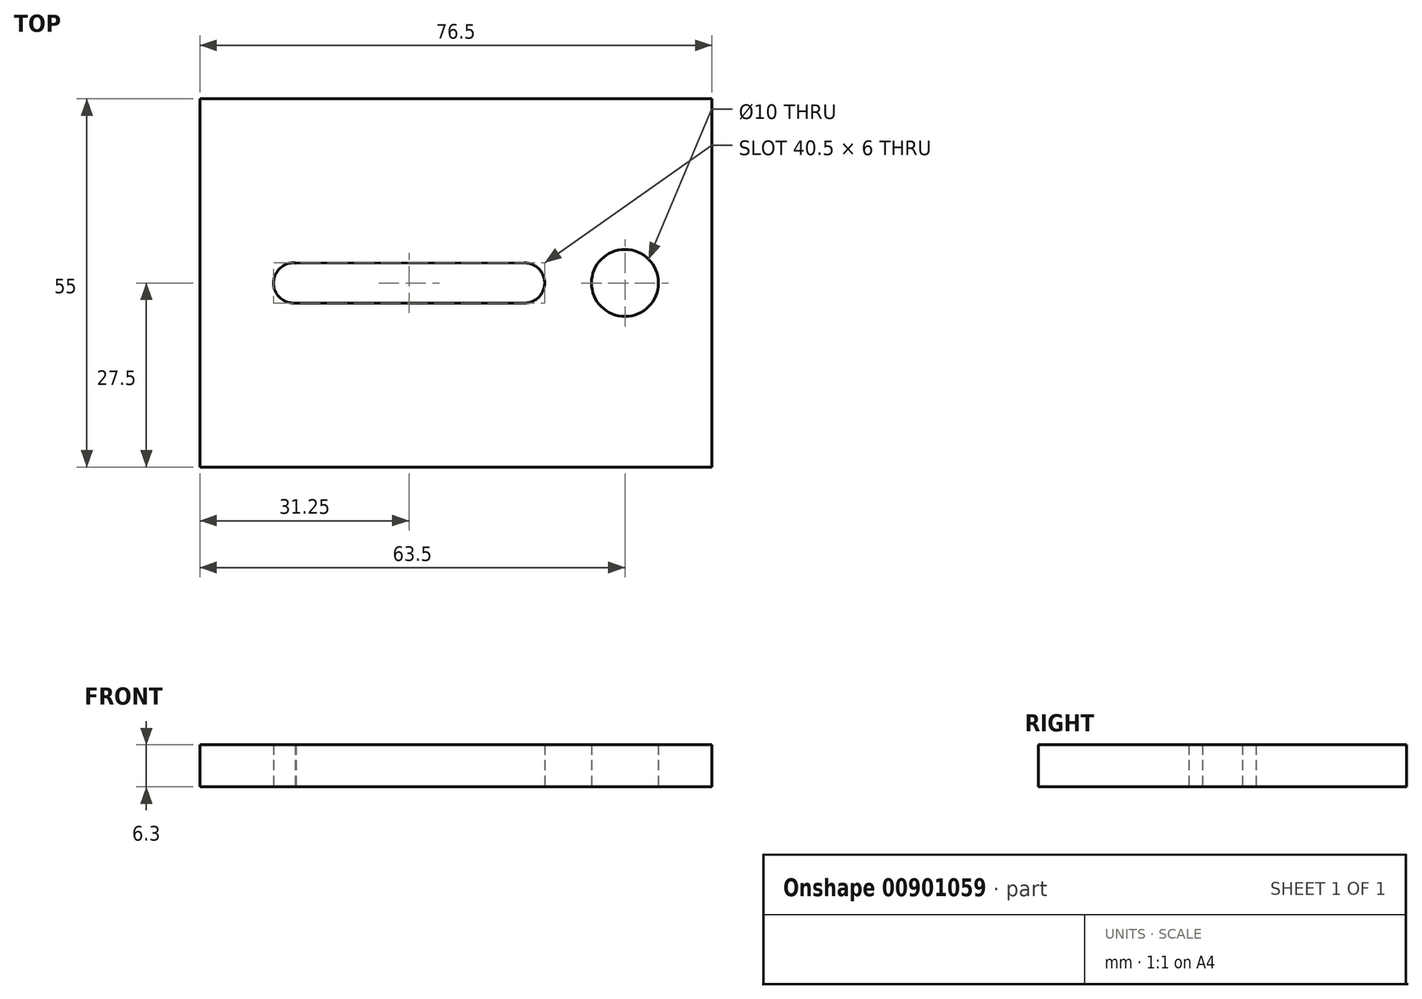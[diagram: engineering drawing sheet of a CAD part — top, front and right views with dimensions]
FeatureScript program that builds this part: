
annotation { "Feature Type Name" : "Feature", "Feature Type Description" : "" }
export const myFeature = defineFeature(function(context is Context, id is Id, definition is map)
    precondition{}
    {
        {
            var Q0;
            Q0=qCreatedBy(makeId("Top.planeOp"),FACE);
            var sketch = newSketch(context, id + "F0", { "sketchPlane" : qUnion([Q0])});
            skLineSegment(sketch, "E0.bottom", {"start": v(38.25, -27.5) * mm, "end": v(-38.25, -27.5) * mm});
            skLineSegment(sketch, "E0.top", {"start": v(38.25, 27.5) * mm, "end": v(-38.25, 27.5) * mm});
            skLineSegment(sketch, "E0.left", {"start": v(38.25, -27.5) * mm, "end": v(38.25, 27.5) * mm});
            skLineSegment(sketch, "E0.right", {"start": v(-38.25, -27.5) * mm, "end": v(-38.25, 27.5) * mm});
            skPoint(sketch, "E0.middle", {"position": v(0, 0) * mm});
            skCircle(sketch, "E1", {"center": v(25.25, 0) * mm, "radius": 5 * mm});
            skCircle(sketch, "E2", {"center": v(10.25, 0) * mm, "radius": 3 * mm});
            skCircle(sketch, "E3", {"center": v(-24.25, 0) * mm, "radius": 3 * mm});
            skLineSegment(sketch, "E4", {"start": v(-24.62, 2.98) * mm, "end": v(10.25, 3) * mm});
            skLineSegment(sketch, "E5", {"start": v(-24.49, -3) * mm, "end": v(10.25, -3) * mm});
            skSolve(sketch);
        }
        {
            var Q0;
            Q0=makeQuery(id+"F0.imprint","IMPRINT",FACE,{"disambiguationData":[TD([[makeQuery(id+"F0.imprint","IMPRINT",EDGE,{"derivedFrom":sQuery(id+"F0.wireOp",EDGE,"E0.bottom")}),-1.0]])]});
            extrude(context, id + "F1", {"entities" : qUnion([Q0]), "depth" : 6.3 * mm, "offsetDistance" : 25 * mm});
        }
    });
